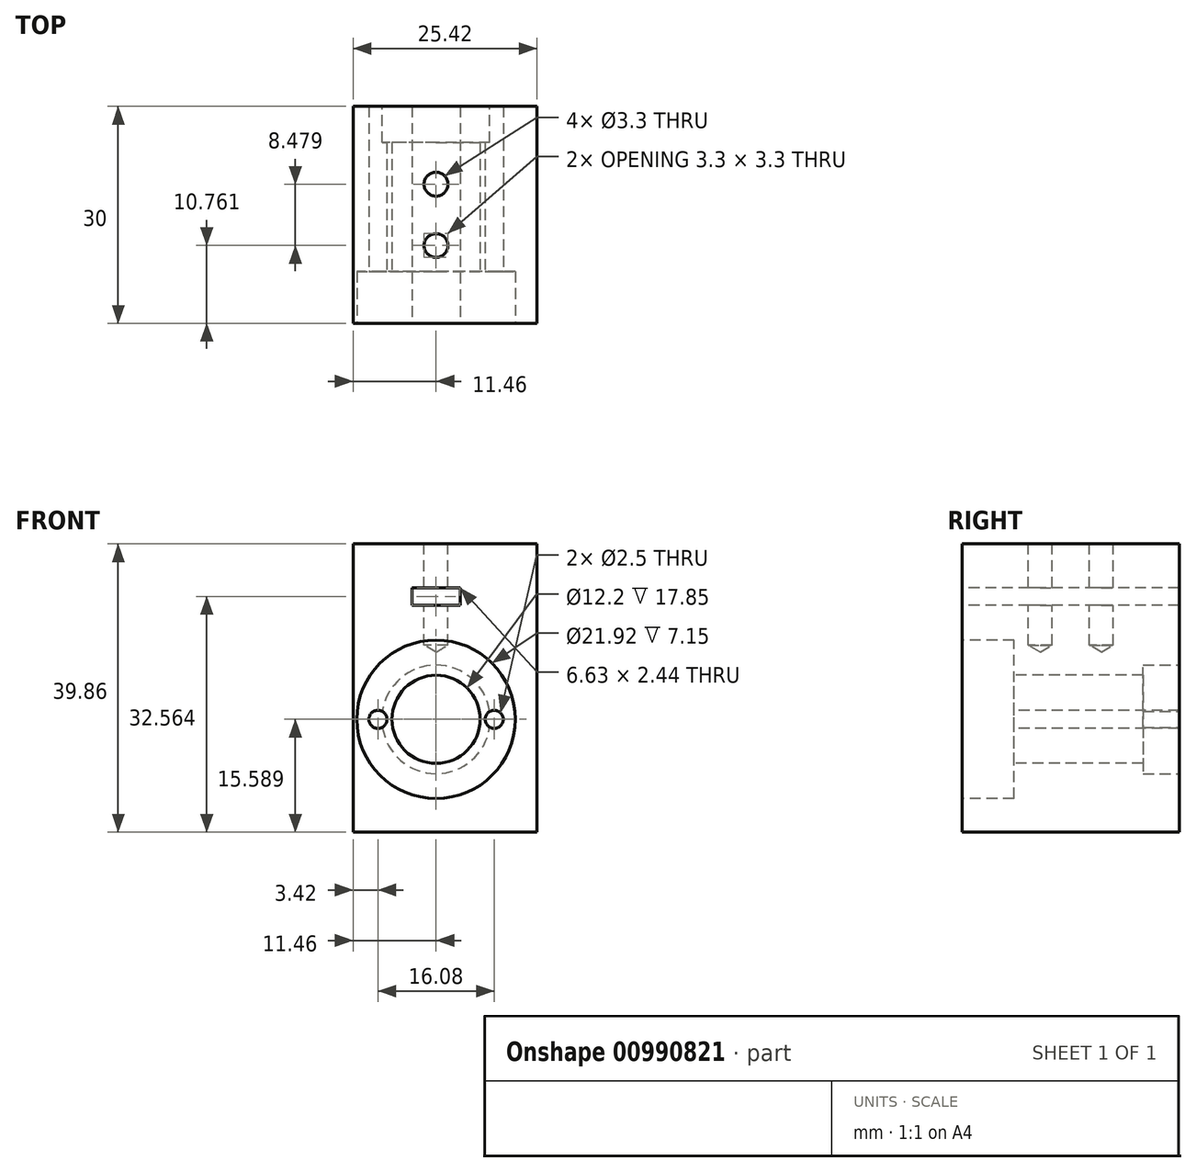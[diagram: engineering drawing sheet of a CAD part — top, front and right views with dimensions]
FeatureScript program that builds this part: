
annotation { "Feature Type Name" : "Feature", "Feature Type Description" : "" }
export const myFeature = defineFeature(function(context is Context, id is Id, definition is map)
    precondition{}
    {
        {
            var Q0;
            Q0=qCreatedBy(makeId("Top.planeOp"),FACE);
            var sketch = newSketch(context, id + "F0", { "sketchPlane" : qUnion([Q0])});
            skLineSegment(sketch, "E0.bottom", {"start": v(12.7, 15) * mm, "end": v(-12.7, 15) * mm});
            skLineSegment(sketch, "E0.top", {"start": v(12.7, -15) * mm, "end": v(-12.7, -15) * mm});
            skLineSegment(sketch, "E0.left", {"start": v(12.7, 15) * mm, "end": v(12.7, -15) * mm});
            skLineSegment(sketch, "E0.right", {"start": v(-12.7, 15) * mm, "end": v(-12.7, -15) * mm});
            skPoint(sketch, "E0.middle", {"position": v(0, 0) * mm});
            skSolve(sketch);
        }
        {
            var Q0;
            Q0=qSketchRegion(id+"F0",true);
            extrude(context, id + "F1", {"entities" : qUnion([Q0]), "depth" : 39.86 * mm, "offsetDistance" : 25 * mm});
        }
        {
            var Q0;
            Q0=makeQuery(id+"F1.opExtrude","CAP_FACE",FACE,{"disambiguationData":[OSD([sQuery(id+"F0.wireOp",EDGE,"E0.bottom"),sQuery(id+"F0.wireOp",EDGE,"E0.top"),sQuery(id+"F0.wireOp",EDGE,"E0.left"),sQuery(id+"F0.wireOp",EDGE,"E0.right")])],"isStart":false});
            var sketch = newSketch(context, id + "F2", { "sketchPlane" : qUnion([Q0])});
            skLineSegment(sketch, "E1", {"start": v(-12.7, 0) * mm, "end": v(-1.25, 0) * mm, "construction": true});
            skLineSegment(sketch, "E2.bottom", {"start": v(-1.25, 4.24) * mm, "end": v(-1.25, 4.24) * mm});
            skLineSegment(sketch, "E2.top", {"start": v(-1.25, -4.24) * mm, "end": v(-1.25, -4.24) * mm});
            skLineSegment(sketch, "E2.left", {"start": v(-1.25, 4.24) * mm, "end": v(-1.25, -4.24) * mm});
            skLineSegment(sketch, "E2.right", {"start": v(-1.25, 4.24) * mm, "end": v(-1.25, -4.24) * mm, "construction": true});
            skPoint(sketch, "E2.middle", {"position": v(-1.25, 0) * mm});
            skPoint(sketch, "E3", {"position": v(-1.25, 4.24) * mm});
            skPoint(sketch, "E4", {"position": v(-1.25, -4.24) * mm});
            skLineSegment(sketch, "E5", {"start": v(-1.25, -4.24) * mm, "end": v(-1.25, -15) * mm, "construction": true});
            skSolve(sketch);
        }
        {
            var Q0;
            Q0=makeQuery(id+"F1.opExtrude","SWEPT_FACE",FACE,{"disambiguationData":[OSD([sQuery(id+"F0.wireOp",EDGE,"E0.top")])]});
            var sketch = newSketch(context, id + "F3", { "sketchPlane" : qUnion([Q0])});
            skLineSegment(sketch, "E6.0.0", {"start": v(-12.7, 39.86) * mm, "end": v(12.7, 39.86) * mm});
            skLineSegment(sketch, "E6.0.2", {"start": v(12.7, 39.86) * mm, "end": v(-12.7, 39.86) * mm});
            skPoint(sketch, "E7.0", {"position": v(-1.25, 39.86) * mm});
            skLineSegment(sketch, "E8", {"start": v(-1.25, 39.86) * mm, "end": v(-1.25, 32.56) * mm, "construction": true});
            skLineSegment(sketch, "E9", {"start": v(-1.25, 39.86) * mm, "end": v(-1.25, 15.59) * mm, "construction": true});
            skLineSegment(sketch, "E10", {"start": v(-1.25, 15.59) * mm, "end": v(-7.35, 15.59) * mm, "construction": true});
            skLineSegment(sketch, "E11", {"start": v(-1.25, 15.59) * mm, "end": v(-12.21, 15.59) * mm, "construction": true});
            skLineSegment(sketch, "E12.bottom", {"start": v(-4.56, 33.79) * mm, "end": v(2.06, 33.79) * mm});
            skLineSegment(sketch, "E12.top", {"start": v(-4.56, 31.34) * mm, "end": v(2.06, 31.34) * mm});
            skLineSegment(sketch, "E12.left", {"start": v(-4.56, 33.79) * mm, "end": v(-4.56, 31.34) * mm});
            skLineSegment(sketch, "E12.right", {"start": v(2.06, 33.79) * mm, "end": v(2.06, 31.34) * mm});
            skPoint(sketch, "E12.middle", {"position": v(-1.25, 32.56) * mm});
            skLineSegment(sketch, "E13.bottom", {"start": v(6.79, 15.59) * mm, "end": v(-9.29, 15.59) * mm});
            skLineSegment(sketch, "E13.top", {"start": v(6.79, 15.59) * mm, "end": v(-9.29, 15.59) * mm, "construction": true});
            skLineSegment(sketch, "E13.left", {"start": v(6.79, 15.59) * mm, "end": v(6.79, 15.59) * mm});
            skLineSegment(sketch, "E13.right", {"start": v(-9.29, 15.59) * mm, "end": v(-9.29, 15.59) * mm});
            skPoint(sketch, "E13.middle", {"position": v(-1.25, 15.59) * mm});
            skPoint(sketch, "E14", {"position": v(-9.29, 15.59) * mm});
            skPoint(sketch, "E15", {"position": v(6.79, 15.59) * mm});
            skCircle(sketch, "E16", {"center": v(-1.25, 15.59) * mm, "radius": 10.96 * mm});
            skSolve(sketch);
        }
        {
            var Q0;
            Q0=sQuery(id+"F2.wireOp",VERTEX,"E3");
            var Q1;
            Q1=sQuery(id+"F2.wireOp",VERTEX,"E4");
            var Q2;
            Q2=makeQuery(id+"F1.opExtrude","SWEPT_BODY",BODY,{"disambiguationData":[OSD([sQuery(id+"F0.wireOp",EDGE,"E0.bottom"),sQuery(id+"F0.wireOp",EDGE,"E0.top"),sQuery(id+"F0.wireOp",EDGE,"E0.left"),sQuery(id+"F0.wireOp",EDGE,"E0.right")])]});
            hole(context, id + "F4", {"style" : HoleStyle.SIMPLE, "endStyle" : HoleEndStyle.BLIND, "standardTappedOrClearance" : lookupTablePath({ "standard" : "ISO", "fit" : "Normal", "size" : "M3", "type" : "Clearance" }), "standardBlindInLast" : lookupTablePath({ "fit" : "Standard", "standard" : "ISO", "size" : "M3", "type" : "Clearance" }), "holeDiameter" : 3.3 * mm, "majorDiameter" : 5 * mm, "holeDepth" : 14 * mm, "tappedDepth" : 12 * mm, "tapClearance" : 3, "startFromSketch" : true, "locations" : qUnion([Q0, Q1]), "scope" : qUnion([Q2])});
        }
        {
            var Q0;
            Q0=makeQuery(id+"F3.imprint","IMPRINT",FACE,{"disambiguationData":[TD([[makeQuery(id+"F3.imprint","IMPRINT",EDGE,{"derivedFrom":sQuery(id+"F3.wireOp",EDGE,"E12.bottom")}),-1.0]])]});
            extrude(context, id + "F5", {"entities" : qUnion([Q0]), "operationType" : NewBodyOperationType.REMOVE, "endBound" : BoundingType.THROUGH_ALL, "oppositeDirection" : true, "depth" : 25 * mm, "offsetDistance" : 25 * mm});
        }
        {
            var Q0;
            Q0=sQuery(id+"F3.wireOp",VERTEX,"E10.start");
            var Q1;
            Q1=makeQuery(id+"F1.opExtrude","SWEPT_BODY",BODY,{"disambiguationData":[OSD([sQuery(id+"F0.wireOp",EDGE,"E0.bottom"),sQuery(id+"F0.wireOp",EDGE,"E0.top"),sQuery(id+"F0.wireOp",EDGE,"E0.left"),sQuery(id+"F0.wireOp",EDGE,"E0.right")])]});
            hole(context, id + "F6", {"style" : HoleStyle.SIMPLE, "endStyle" : HoleEndStyle.THROUGH, "holeDiameter" : 12.2 * mm, "majorDiameter" : 5 * mm, "tappedDepth" : 12 * mm, "tapClearance" : 3, "startFromSketch" : true, "locations" : qUnion([Q0]), "scope" : qUnion([Q1])});
        }
        {
            var Q0;
            Q0=sQuery(id+"F3.wireOp",VERTEX,"E14");
            var Q1;
            Q1=sQuery(id+"F3.wireOp",VERTEX,"E15");
            var Q2;
            Q2=makeQuery(id+"F1.opExtrude","SWEPT_BODY",BODY,{"disambiguationData":[OSD([sQuery(id+"F0.wireOp",EDGE,"E0.bottom"),sQuery(id+"F0.wireOp",EDGE,"E0.top"),sQuery(id+"F0.wireOp",EDGE,"E0.left"),sQuery(id+"F0.wireOp",EDGE,"E0.right")])]});
            hole(context, id + "F7", {"style" : HoleStyle.SIMPLE, "endStyle" : HoleEndStyle.THROUGH, "standardTappedOrClearance" : lookupTablePath({ "standard" : "ISO", "engagement" : "75%", "pitch" : "0.5 mm", "size" : "M3", "type" : "Tapped" }), "standardBlindInLast" : lookupTablePath({ "standard" : "ISO", "engagement" : "75%", "pitch" : "0.5 mm", "size" : "M3", "type" : "Tapped" }), "holeDiameter" : 2.5 * mm, "majorDiameter" : 3 * mm, "showTappedDepth" : true, "tappedDepth" : 12 * mm, "tapClearance" : 3, "startFromSketch" : true, "locations" : qUnion([Q0, Q1]), "scope" : qUnion([Q2])});
        }
        {
            var Q0;
            Q0=makeQuery(id+"F3.imprint","IMPRINT",FACE,{"disambiguationData":[TD([[makeQuery(id+"F3.imprint","IMPRINT",EDGE,{"derivedFrom":sQuery(id+"F3.wireOp",EDGE,"E16")}),1.0]])]});
            extrude(context, id + "F8", {"entities" : qUnion([Q0]), "operationType" : NewBodyOperationType.REMOVE, "oppositeDirection" : true, "depth" : 7.15 * mm, "offsetDistance" : 25 * mm});
        }
        {
            var Q0;
            Q0=makeQuery(id+"F1.opExtrude","SWEPT_FACE",FACE,{"disambiguationData":[OSD([sQuery(id+"F0.wireOp",EDGE,"E0.bottom")])]});
            var sketch = newSketch(context, id + "F9", { "sketchPlane" : qUnion([Q0])});
            skPoint(sketch, "E17.0", {"position": v(1.25, 15.59) * mm});
            skCircle(sketch, "E18", {"center": v(1.25, 15.59) * mm, "radius": 7.5 * mm});
            skSolve(sketch);
        }
        {
            var Q0;
            Q0=qSketchRegion(id+"F9",true);
            extrude(context, id + "F10", {"entities" : qUnion([Q0]), "operationType" : NewBodyOperationType.REMOVE, "oppositeDirection" : true, "depth" : 5 * mm, "offsetDistance" : 25 * mm});
        }
    });
